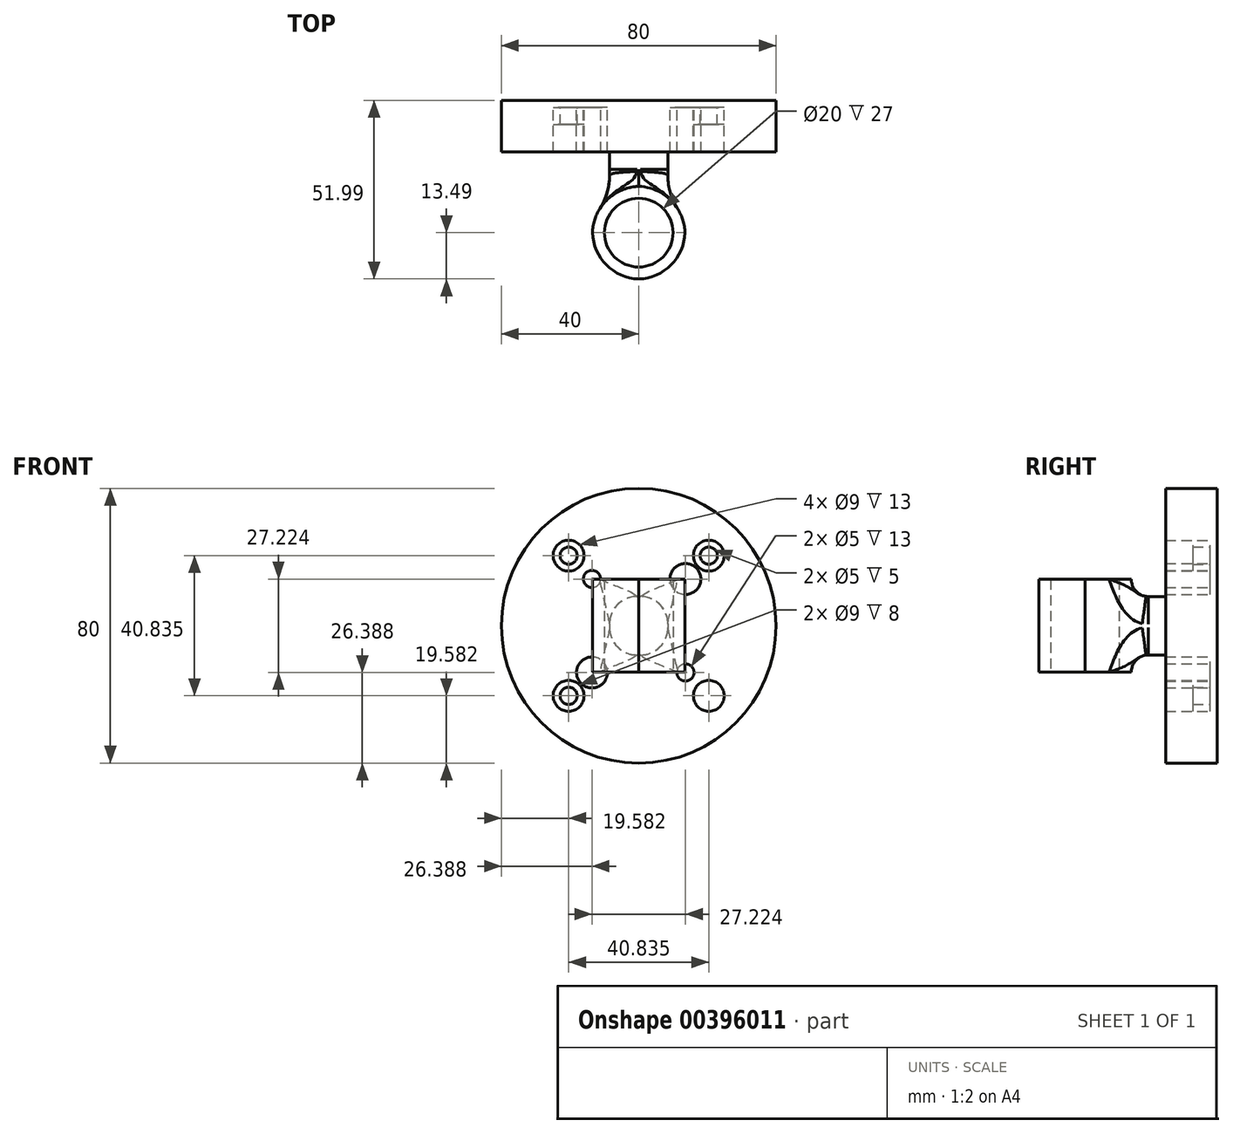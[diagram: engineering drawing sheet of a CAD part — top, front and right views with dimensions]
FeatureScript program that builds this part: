
annotation { "Feature Type Name" : "Feature", "Feature Type Description" : "" }
export const myFeature = defineFeature(function(context is Context, id is Id, definition is map)
    precondition{}
    {
        {
            var Q0;
            Q0=qCreatedBy(makeId("Front.planeOp"),FACE);
            var sketch = newSketch(context, id + "F0", { "sketchPlane" : qUnion([Q0])});
            skCircle(sketch, "E0", {"center": v(0, 0) * mm, "radius": 40 * mm});
            skSolve(sketch);
        }
        {
            var Q0;
            Q0=makeQuery(id+"F0.imprint","IMPRINT",FACE,{"disambiguationData":[TD([[makeQuery(id+"F0.imprint","IMPRINT",EDGE,{"derivedFrom":sQuery(id+"F0.wireOp",EDGE,"E0")}),1.0]])]});
            extrude(context, id + "F1", {"entities" : qUnion([Q0]), "depth" : 2 * mm});
        }
        {
            var Q0;
            Q0=makeQuery(id+"F1.opExtrude","CAP_FACE",FACE,{"disambiguationData":[OSD([sQuery(id+"F0.wireOp",EDGE,"E0")])],"isStart":false});
            var sketch = newSketch(context, id + "F2", { "sketchPlane" : qUnion([Q0])});
            skCircle(sketch, "E1", {"center": v(0, 0) * mm, "radius": 38.5 * mm});
            skLineSegment(sketch, "E2", {"start": v(0, 48.56) * mm, "end": v(0, -46.67) * mm, "construction": true});
            skPoint(sketch, "E3", {"position": v(-13.61, 13.61) * mm});
            skPoint(sketch, "E4", {"position": v(-20.42, 20.42) * mm});
            skLineSegment(sketch, "E5", {"start": v(-38.5, 0) * mm, "end": v(38.5, 0) * mm, "construction": true});
            skPoint(sketch, "E6.MirrorP", {"position": v(13.61, 13.61) * mm});
            skPoint(sketch, "E7.MirrorP", {"position": v(20.42, 20.42) * mm});
            skPoint(sketch, "E8.MirrorP", {"position": v(-13.61, -13.61) * mm});
            skPoint(sketch, "E9.MirrorP", {"position": v(-20.42, -20.42) * mm});
            skPoint(sketch, "E10.MirrorP", {"position": v(13.61, -13.61) * mm});
            skPoint(sketch, "E11.MirrorP", {"position": v(20.42, -20.42) * mm});
            skCircle(sketch, "E12", {"center": v(20.42, 20.42) * mm, "radius": 2.5 * mm});
            skCircle(sketch, "E13.MirrorC", {"center": v(-20.42, 20.42) * mm, "radius": 2.5 * mm});
            skCircle(sketch, "E14.MirrorC", {"center": v(-20.42, -20.42) * mm, "radius": 2.5 * mm});
            skCircle(sketch, "E15.MirrorC", {"center": v(20.42, -20.42) * mm, "radius": 2.5 * mm});
            skCircle(sketch, "E16.0", {"center": v(-20.42, 20.42) * mm, "radius": 4.5 * mm});
            skCircle(sketch, "E17", {"center": v(-13.61, 13.61) * mm, "radius": 2.5 * mm});
            skCircle(sketch, "E18.0", {"center": v(-13.61, 13.61) * mm, "radius": 4.5 * mm});
            skCircle(sketch, "E19.MirrorC", {"center": v(13.61, 13.61) * mm, "radius": 4.5 * mm});
            skCircle(sketch, "E20.MirrorC", {"center": v(13.61, 13.61) * mm, "radius": 2.5 * mm});
            skCircle(sketch, "E21.MirrorC", {"center": v(20.42, 20.42) * mm, "radius": 4.5 * mm});
            skCircle(sketch, "E22.MirrorC", {"center": v(-13.61, -13.61) * mm, "radius": 4.5 * mm});
            skCircle(sketch, "E23.MirrorC", {"center": v(-13.61, -13.61) * mm, "radius": 2.5 * mm});
            skCircle(sketch, "E24.MirrorC", {"center": v(-20.42, -20.42) * mm, "radius": 4.5 * mm});
            skCircle(sketch, "E25.MirrorC", {"center": v(13.61, -13.61) * mm, "radius": 4.5 * mm});
            skCircle(sketch, "E26.MirrorC", {"center": v(13.61, -13.61) * mm, "radius": 2.5 * mm});
            skCircle(sketch, "E27.MirrorC", {"center": v(20.42, -20.42) * mm, "radius": 4.5 * mm});
            skSolve(sketch);
        }
        {
            var Q0;
            Q0=makeQuery(id+"F2.imprint","IMPRINT",FACE,{"disambiguationData":[TD([[makeQuery(id+"F2.imprint","IMPRINT",EDGE,{"derivedFrom":sQuery(id+"F2.wireOp",EDGE,"E1")}),-1.0]])]});
            extrude(context, id + "F3", {"entities" : qUnion([Q0]), "operationType" : NewBodyOperationType.ADD, "depth" : 10 * mm});
        }
        {
            var Q0;
            Q0=makeQuery(id+"F2.imprint","IMPRINT",FACE,{"disambiguationData":[TD([[makeQuery(id+"F2.imprint","IMPRINT",EDGE,{"derivedFrom":sQuery(id+"F2.wireOp",EDGE,"E13.MirrorC")}),1.0]])]});
            var Q1;
            Q1=makeQuery(id+"F2.imprint","IMPRINT",FACE,{"disambiguationData":[TD([[makeQuery(id+"F2.imprint","IMPRINT",EDGE,{"derivedFrom":sQuery(id+"F2.wireOp",EDGE,"E12")}),-1.0]])]});
            var Q2;
            Q2=makeQuery(id+"F2.imprint","IMPRINT",FACE,{"disambiguationData":[TD([[makeQuery(id+"F2.imprint","IMPRINT",EDGE,{"derivedFrom":sQuery(id+"F2.wireOp",EDGE,"E27.MirrorC")}),-1.0]])]});
            var Q3;
            Q3=makeQuery(id+"F2.imprint","IMPRINT",FACE,{"disambiguationData":[TD([[makeQuery(id+"F2.imprint","IMPRINT",EDGE,{"derivedFrom":sQuery(id+"F2.wireOp",EDGE,"E24.MirrorC")}),1.0]])]});
            extrude(context, id + "F4", {"entities" : qUnion([Q0, Q1, Q2, Q3]), "operationType" : NewBodyOperationType.ADD, "depth" : 5 * mm});
        }
        {
            var Q0;
            Q0=makeQuery(id+"F2.imprint","IMPRINT",FACE,{"disambiguationData":[TD([[makeQuery(id+"F2.imprint","IMPRINT",EDGE,{"derivedFrom":sQuery(id+"F2.wireOp",EDGE,"E17")}),-1.0]])]});
            var Q1;
            Q1=makeQuery(id+"F2.imprint","IMPRINT",FACE,{"disambiguationData":[TD([[makeQuery(id+"F2.imprint","IMPRINT",EDGE,{"derivedFrom":sQuery(id+"F2.wireOp",EDGE,"E19.MirrorC")}),-1.0]])]});
            var Q2;
            Q2=makeQuery(id+"F2.imprint","IMPRINT",FACE,{"disambiguationData":[TD([[makeQuery(id+"F2.imprint","IMPRINT",EDGE,{"derivedFrom":sQuery(id+"F2.wireOp",EDGE,"E25.MirrorC")}),1.0]])]});
            var Q3;
            Q3=makeQuery(id+"F2.imprint","IMPRINT",FACE,{"disambiguationData":[TD([[makeQuery(id+"F2.imprint","IMPRINT",EDGE,{"derivedFrom":sQuery(id+"F2.wireOp",EDGE,"E22.MirrorC")}),-1.0]])]});
            extrude(context, id + "F5", {"entities" : qUnion([Q0, Q1, Q2, Q3]), "operationType" : NewBodyOperationType.ADD, "depth" : 10 * mm});
        }
        {
            var Q0;
            Q0=makeQuery(id+"F3.opExtrude","CAP_FACE",FACE,{"disambiguationData":[OSD([sQuery(id+"F0.wireOp",EDGE,"E0"),sQuery(id+"F2.wireOp",EDGE,"E1")])],"isStart":false});
            var sketch = newSketch(context, id + "F6", { "sketchPlane" : qUnion([Q0])});
            skCircle(sketch, "E28", {"center": v(0, 0) * mm, "radius": 40 * mm});
            skCircle(sketch, "E29", {"center": v(0, 0) * mm, "radius": 38.5 * mm});
            skCircle(sketch, "E30", {"center": v(0, 0) * mm, "radius": 37 * mm});
            skSolve(sketch);
        }
        {
            var Q0;
            Q0=makeQuery(id+"F6.imprint","IMPRINT",FACE,{"disambiguationData":[TD([[makeQuery(id+"F6.imprint","IMPRINT",EDGE,{"derivedFrom":sQuery(id+"F6.wireOp",EDGE,"E29")}),1.0]])]});
            extrude(context, id + "F7", {"entities" : qUnion([Q0]), "oppositeDirection" : true, "depth" : 3 * mm});
        }
        {
            var Q0;
            Q0=makeQuery(id+"F6.imprint","IMPRINT",FACE,{"disambiguationData":[TD([[makeQuery(id+"F6.imprint","IMPRINT",EDGE,{"derivedFrom":sQuery(id+"F6.wireOp",EDGE,"E30")}),1.0]])]});
            var Q1;
            Q1=makeQuery(id+"F6.imprint","IMPRINT",FACE,{"disambiguationData":[TD([[makeQuery(id+"F6.imprint","IMPRINT",EDGE,{"derivedFrom":sQuery(id+"F6.wireOp",EDGE,"E29")}),1.0]])]});
            var Q2;
            Q2=makeQuery(id+"F6.imprint","IMPRINT",FACE,{"disambiguationData":[TD([[makeQuery(id+"F6.imprint","IMPRINT",EDGE,{"derivedFrom":sQuery(id+"F6.wireOp",EDGE,"E28")}),1.0]])]});
            extrude(context, id + "F8", {"entities" : qUnion([Q0, Q1, Q2]), "operationType" : NewBodyOperationType.ADD, "depth" : 3 * mm});
        }
        {
            var Q0;
            Q0=makeQuery(id+"F8.opExtrude","CAP_FACE",FACE,{"disambiguationData":[OSD([sQuery(id+"F6.wireOp",EDGE,"E28")])],"isStart":false});
            var sketch = newSketch(context, id + "F9", { "sketchPlane" : qUnion([Q0])});
            skLineSegment(sketch, "E31.bottom", {"start": v(8.5, 8.5) * mm, "end": v(-8.5, 8.5) * mm});
            skLineSegment(sketch, "E31.top", {"start": v(8.5, -8.5) * mm, "end": v(-8.5, -8.5) * mm});
            skLineSegment(sketch, "E31.left", {"start": v(8.5, 8.5) * mm, "end": v(8.5, -8.5) * mm});
            skLineSegment(sketch, "E31.right", {"start": v(-8.5, 8.5) * mm, "end": v(-8.5, -8.5) * mm});
            skPoint(sketch, "E31.middle", {"position": v(0, 0) * mm});
            skSolve(sketch);
        }
        {
            var Q0;
            Q0=makeQuery(id+"F9.imprint","IMPRINT",FACE,{"disambiguationData":[TD([[makeQuery(id+"F9.imprint","IMPRINT",EDGE,{"derivedFrom":sQuery(id+"F9.wireOp",EDGE,"oU5cO6TK-QLEp-UcP5-oZvJ-mS3zXpuoh6tz")}),1.0]])]});
            var Q1;
            Q1=makeQuery(id+"F9.imprint","IMPRINT",FACE,{"disambiguationData":[TD([[makeQuery(id+"F9.imprint","IMPRINT",EDGE,{"derivedFrom":sQuery(id+"F9.wireOp",EDGE,"E31.bottom")}),1.0]])]});
            extrude(context, id + "F10", {"entities" : qUnion([Q0, Q1]), "operationType" : NewBodyOperationType.ADD, "depth" : 10 * mm});
        }
        {
            var Q0;
            Q0=makeQuery(id+"F10.opExtrude","CAP_FACE",FACE,{"disambiguationData":[OSD([sQuery(id+"F9.wireOp",EDGE,"E31.bottom"),sQuery(id+"F9.wireOp",EDGE,"E31.top"),sQuery(id+"F9.wireOp",EDGE,"E31.left"),sQuery(id+"F9.wireOp",EDGE,"E31.right")])],"isStart":false});
            var sketch = newSketch(context, id + "F11", { "sketchPlane" : qUnion([Q0])});
            skLineSegment(sketch, "E32.0", {"start": v(-13.5, -13.5) * mm, "end": v(13.5, -13.5) * mm});
            skLineSegment(sketch, "E32.1", {"start": v(-13.5, 13.5) * mm, "end": v(-13.5, -13.5) * mm});
            skLineSegment(sketch, "E32.2", {"start": v(13.5, 13.5) * mm, "end": v(-13.5, 13.5) * mm});
            skLineSegment(sketch, "E32.3", {"start": v(13.5, -13.5) * mm, "end": v(13.5, 13.5) * mm});
            skSolve(sketch);
        }
        {
            var Q0;
            Q0=makeQuery(id+"F11.imprint","IMPRINT",FACE,{"disambiguationData":[TD([[makeQuery(id+"F11.imprint","IMPRINT",EDGE,{"derivedFrom":makeQuery(id+"F10.opExtrude","CAP_EDGE",EDGE,{"disambiguationData":[OSD([sQuery(id+"F9.wireOp",EDGE,"E31.bottom")])],"isStart":false})}),1.0]])]});
            var Q1;
            Q1=makeQuery(id+"F11.imprint","IMPRINT",FACE,{"disambiguationData":[TD([[makeQuery(id+"F11.imprint","IMPRINT",EDGE,{"derivedFrom":sQuery(id+"F11.wireOp",EDGE,"E32.0")}),1.0]])]});
            extrude(context, id + "F12", {"entities" : qUnion([Q0, Q1]), "operationType" : NewBodyOperationType.ADD, "depth" : 27 * mm});
        }
        {
            var Q0;
            Q0=makeQuery(id+"F12.opExtrude","SWEPT_FACE",FACE,{"disambiguationData":[OSD([sQuery(id+"F11.wireOp",EDGE,"E32.0")])]});
            var sketch = newSketch(context, id + "F13", { "sketchPlane" : qUnion([Q0])});
            skLineSegment(sketch, "E33", {"start": v(-13.5, 52) * mm, "end": v(13.5, 25) * mm, "construction": true});
            skCircle(sketch, "E34", {"center": v(0, 38.5) * mm, "radius": 10 * mm});
            skLineSegment(sketch, "E35", {"start": v(0, 25) * mm, "end": v(0, 38.5) * mm, "construction": true});
            skSolve(sketch);
        }
        {
            var Q0;
            Q0=makeQuery(id+"F13.imprint","IMPRINT",FACE,{"disambiguationData":[TD([[makeQuery(id+"F13.imprint","IMPRINT",EDGE,{"derivedFrom":sQuery(id+"F13.wireOp",EDGE,"E34")}),1.0]])]});
            extrude(context, id + "F14", {"entities" : qUnion([Q0]), "operationType" : NewBodyOperationType.REMOVE, "endBound" : BoundingType.UP_TO_NEXT, "oppositeDirection" : true, "depth" : 25 * mm});
        }
        {
            var Q0;
            Q0=makeQuery(id+"F12.opExtrude","CAP_EDGE",EDGE,{"disambiguationData":[OSD([sQuery(id+"F11.wireOp",EDGE,"E32.3")])],"isStart":true});
            var Q1;
            Q1=makeQuery(id+"F12.opExtrude","CAP_EDGE",EDGE,{"disambiguationData":[OSD([sQuery(id+"F11.wireOp",EDGE,"E32.1")])],"isStart":true});
            var Q2;
            Q2=makeQuery(id+"F12.opExtrude","CAP_EDGE",EDGE,{"disambiguationData":[OSD([sQuery(id+"F11.wireOp",EDGE,"E32.3")])],"isStart":false});
            var Q3;
            Q3=makeQuery(id+"F12.opExtrude","CAP_EDGE",EDGE,{"disambiguationData":[OSD([sQuery(id+"F11.wireOp",EDGE,"E32.1")])],"isStart":false});
            fillet(context, id + "F15", {"entities" : qUnion([Q0, Q1, Q2, Q3]), "radius" : 14 * mm, "tangentPropagation" : true, "allowEdgeOverflow" : false});
        }
        {
            var Q0;
            Q0=makeQuery(id+"F15.opFillet","BLEND_EDGE",EDGE,{"blendedFrom":[makeQuery(id+"F12.opExtrude","CAP_EDGE",EDGE,{"disambiguationData":[OSD([sQuery(id+"F11.wireOp",EDGE,"E32.1")])],"isStart":true}),makeQuery(id+"F10.opExtrude","SWEPT_FACE",FACE,{"disambiguationData":[OSD([sQuery(id+"F9.wireOp",EDGE,"E31.right")])]})],"blendedInto":[makeQuery(id+"F10.opExtrude","SWEPT_FACE",FACE,{"disambiguationData":[OSD([sQuery(id+"F9.wireOp",EDGE,"E31.right")])]})]});
            var Q1;
            Q1=makeQuery(id+"F15.opFillet","BLEND_EDGE",EDGE,{"blendedFrom":[makeQuery(id+"F12.opExtrude","CAP_EDGE",EDGE,{"disambiguationData":[OSD([sQuery(id+"F11.wireOp",EDGE,"E32.3")])],"isStart":true}),makeQuery(id+"F10.opExtrude","SWEPT_FACE",FACE,{"disambiguationData":[OSD([sQuery(id+"F9.wireOp",EDGE,"E31.left")])]})],"blendedInto":[makeQuery(id+"F10.opExtrude","SWEPT_FACE",FACE,{"disambiguationData":[OSD([sQuery(id+"F9.wireOp",EDGE,"E31.left")])]})]});
            fillet(context, id + "F16", {"entities" : qUnion([Q0, Q1]), "radius" : 18 * mm, "tangentPropagation" : true, "allowEdgeOverflow" : false});
        }
        {
            var Q0;
            Q0=makeQuery(id+"F15.opFillet","BLEND_EDGE",EDGE,{"blendedFrom":[makeQuery(id+"F12.opExtrude","CAP_EDGE",EDGE,{"disambiguationData":[OSD([sQuery(id+"F11.wireOp",EDGE,"E32.3")])],"isStart":true}),makeQuery(id+"F10.opExtrude","SWEPT_FACE",FACE,{"disambiguationData":[OSD([sQuery(id+"F9.wireOp",EDGE,"E31.top")])]})],"blendedInto":[makeQuery(id+"F10.opExtrude","SWEPT_FACE",FACE,{"disambiguationData":[OSD([sQuery(id+"F9.wireOp",EDGE,"E31.top")])]})]});
            var Q1;
            Q1=makeQuery(id+"F15.opFillet","BLEND_EDGE",EDGE,{"blendedFrom":[makeQuery(id+"F12.opExtrude","CAP_EDGE",EDGE,{"disambiguationData":[OSD([sQuery(id+"F11.wireOp",EDGE,"E32.3")])],"isStart":true}),makeQuery(id+"F10.opExtrude","SWEPT_FACE",FACE,{"disambiguationData":[OSD([sQuery(id+"F9.wireOp",EDGE,"E31.bottom")])]})],"blendedInto":[makeQuery(id+"F10.opExtrude","SWEPT_FACE",FACE,{"disambiguationData":[OSD([sQuery(id+"F9.wireOp",EDGE,"E31.bottom")])]})]});
            fillet(context, id + "F17", {"entities" : qUnion([Q0, Q1]), "radius" : 5 * mm, "tangentPropagation" : true, "allowEdgeOverflow" : false});
        }
        {
            var Q0;
            Q0=makeQuery(id+"F10.opExtrude","SWEPT_EDGE",EDGE,{"disambiguationData":[OSD([sQuery(id+"F9.wireOp",EDGE,"E31.top"),sQuery(id+"F9.wireOp",EDGE,"E31.left")])]});
            var Q1;
            Q1=makeQuery(id+"F10.opExtrude","SWEPT_EDGE",EDGE,{"disambiguationData":[OSD([sQuery(id+"F9.wireOp",EDGE,"E31.bottom"),sQuery(id+"F9.wireOp",EDGE,"E31.left")])]});
            var Q2;
            Q2=makeQuery(id+"F10.opExtrude","SWEPT_EDGE",EDGE,{"disambiguationData":[OSD([sQuery(id+"F9.wireOp",EDGE,"E31.top"),sQuery(id+"F9.wireOp",EDGE,"E31.right")])]});
            var Q3;
            Q3=makeQuery(id+"F10.opExtrude","SWEPT_EDGE",EDGE,{"disambiguationData":[OSD([sQuery(id+"F9.wireOp",EDGE,"E31.bottom"),sQuery(id+"F9.wireOp",EDGE,"E31.right")])]});
            fillet(context, id + "F18", {"entities" : qUnion([Q0, Q1, Q2, Q3]), "radius" : 8 * mm, "tangentPropagation" : true, "allowEdgeOverflow" : false});
        }
    });
